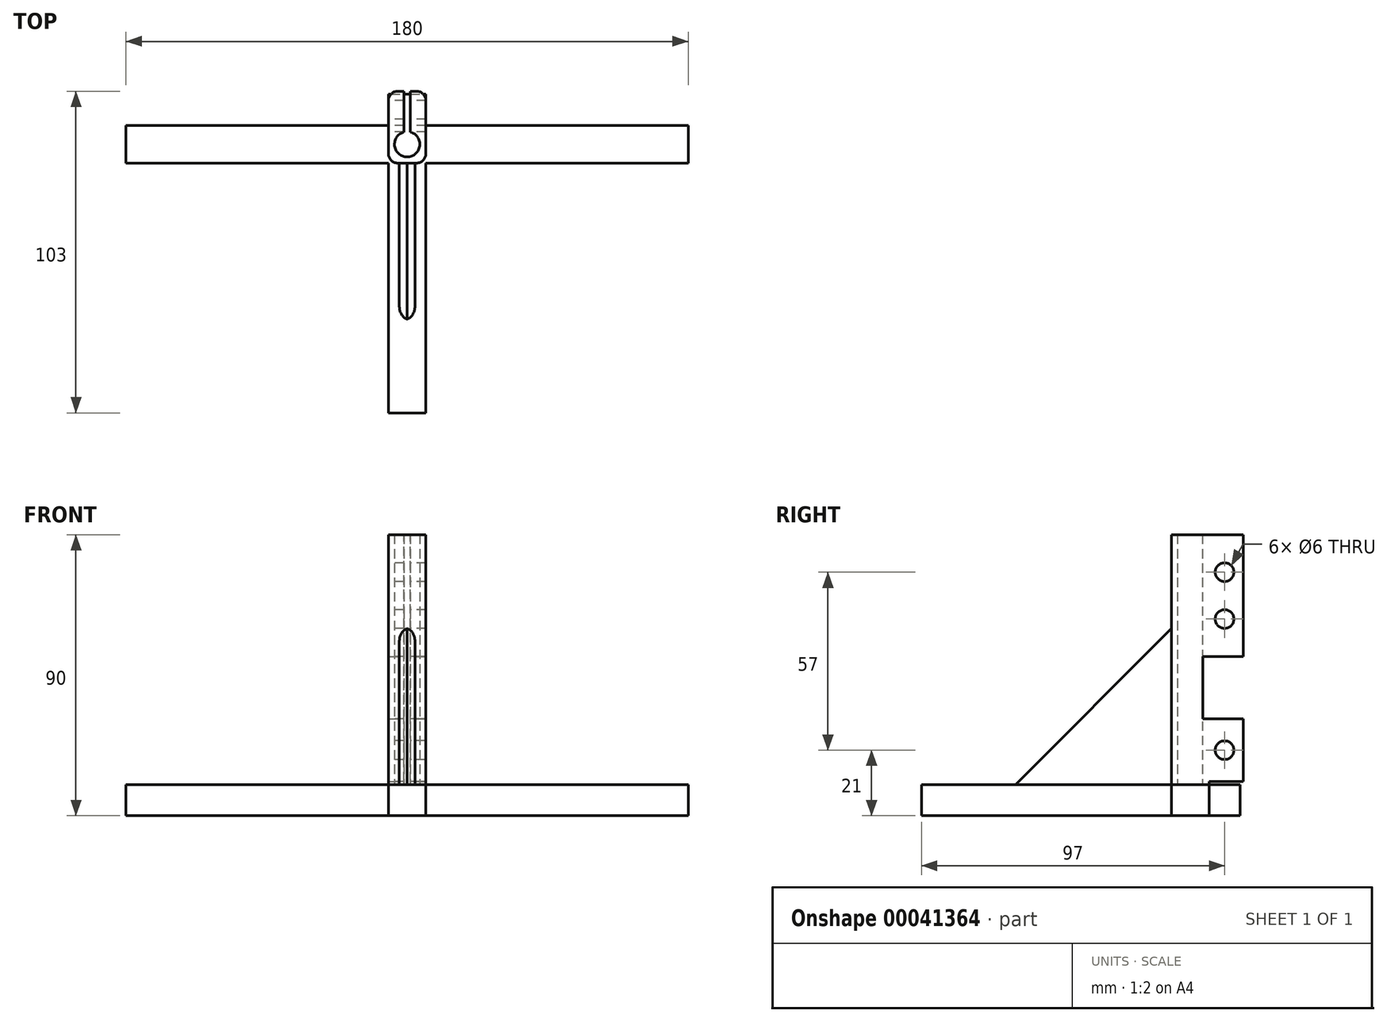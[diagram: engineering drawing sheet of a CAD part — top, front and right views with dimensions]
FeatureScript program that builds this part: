
annotation { "Feature Type Name" : "Feature", "Feature Type Description" : "" }
export const myFeature = defineFeature(function(context is Context, id is Id, definition is map)
    precondition{}
    {
        {
            var Q0;
            Q0=qCreatedBy(makeId("Top.planeOp"),FACE);
            var sketch = newSketch(context, id + "F0", { "sketchPlane" : qUnion([Q0])});
            skLineSegment(sketch, "E0", {"start": v(0, 22) * mm, "end": v(-6, 22) * mm});
            skLineSegment(sketch, "E1", {"start": v(-6, 22) * mm, "end": v(-6, 12) * mm});
            skLineSegment(sketch, "E2", {"start": v(-6, 12) * mm, "end": v(-90, 12) * mm});
            skLineSegment(sketch, "E3", {"start": v(-90, 12) * mm, "end": v(-90, 0) * mm});
            skLineSegment(sketch, "E4.MirrorCS", {"start": v(90, 12) * mm, "end": v(90, 0) * mm});
            skLineSegment(sketch, "E5.MirrorCS", {"start": v(6, 12) * mm, "end": v(90, 12) * mm});
            skLineSegment(sketch, "E6.MirrorCS", {"start": v(0, 22) * mm, "end": v(6, 22) * mm});
            skLineSegment(sketch, "E7.MirrorCS", {"start": v(6, 22) * mm, "end": v(6, 12) * mm});
            skLineSegment(sketch, "E8", {"start": v(-90, 0) * mm, "end": v(-6, 0) * mm});
            skLineSegment(sketch, "E9", {"start": v(-6, 0) * mm, "end": v(-6, -80) * mm});
            skLineSegment(sketch, "E10", {"start": v(-6, -80) * mm, "end": v(6, -80) * mm});
            skLineSegment(sketch, "E11", {"start": v(6, -80) * mm, "end": v(6, 0) * mm});
            skLineSegment(sketch, "E12", {"start": v(6, 0) * mm, "end": v(90, 0) * mm});
            skSolve(sketch);
        }
        {
            var Q0;
            Q0 = qSketchRegion(id + "F0", true);
            extrude(context, id + "F1", {"entities" : qUnion([Q0]), "depth" : 10 * mm});
        }
        {
            var Q0;
            Q0=makeQuery(id+"F1.opExtrude","CAP_FACE",FACE,{"disambiguationData":[OSD([sQuery(id+"F0.wireOp",EDGE,"E0"),sQuery(id+"F0.wireOp",EDGE,"E1"),sQuery(id+"F0.wireOp",EDGE,"E2"),sQuery(id+"F0.wireOp",EDGE,"E3"),sQuery(id+"F0.wireOp",EDGE,"198ae0ac-48d3-4eb9-aa4b-bc29fb24422c"),sQuery(id+"F0.wireOp",EDGE,"9f05f684-929d-4ba8-9fca-e720e47223410.MirrorCS"),sQuery(id+"F0.wireOp",EDGE,"E4.MirrorCS"),sQuery(id+"F0.wireOp",EDGE,"E5.MirrorCS"),sQuery(id+"F0.wireOp",EDGE,"E6.MirrorCS"),sQuery(id+"F0.wireOp",EDGE,"E7.MirrorCS")])],"isStart":false});
            var sketch = newSketch(context, id + "F2", { "sketchPlane" : qUnion([Q0])});
            skSolve(sketch);
        }
        {
            var Q0;
            Q0=makeQuery(id+"F2.imprint","IMPRINT",FACE,{"disambiguationData":[TD([[makeQuery(id+"F2.imprint","IMPRINT",EDGE,{"derivedFrom":makeQuery(id+"F1.opExtrude","CAP_EDGE",EDGE,{"disambiguationData":[OSD([sQuery(id+"F0.wireOp",EDGE,"E1")])],"isStart":false})}),1.0]])]});
            var sketch = newSketch(context, id + "F3", { "sketchPlane" : qUnion([Q0])});
            skLineSegment(sketch, "E13.rect.bottom", {"start": v(-6, 0) * mm, "end": v(6, 0) * mm});
            skLineSegment(sketch, "E13.rect.top", {"start": v(-6, 23) * mm, "end": v(6, 23) * mm});
            skLineSegment(sketch, "E13.rect.left", {"start": v(-6, 0) * mm, "end": v(-6, 23) * mm});
            skLineSegment(sketch, "E13.rect.right", {"start": v(6, 0) * mm, "end": v(6, 23) * mm});
            skPoint(sketch, "E13.rect.middle", {"position": v(0, 11.5) * mm});
            skCircle(sketch, "E14", {"center": v(0, 6) * mm, "radius": 4.05 * mm});
            skSolve(sketch);
        }
        {
            var Q0;
            Q0 = qSketchRegion(id + "F3", true);
            extrude(context, id + "F4", {"entities" : qUnion([Q0]), "operationType" : NewBodyOperationType.ADD, "depth" : 80 * mm});
        }
        {
            var Q0;
            Q0=makeQuery(id+"F2.imprint","IMPRINT",FACE,{"disambiguationData":[TD([[makeQuery(id+"F2.imprint","IMPRINT",EDGE,{"derivedFrom":makeQuery(id+"F1.opExtrude","CAP_EDGE",EDGE,{"disambiguationData":[OSD([sQuery(id+"F0.wireOp",EDGE,"E1")])],"isStart":false})}),1.0]])]});
            var sketch = newSketch(context, id + "F5", { "sketchPlane" : qUnion([Q0])});
            skLineSegment(sketch, "E15.rect.bottom", {"start": v(1, 6.26) * mm, "end": v(-1, 6.26) * mm});
            skLineSegment(sketch, "E15.rect.top", {"start": v(1, 45.32) * mm, "end": v(-1, 45.32) * mm});
            skLineSegment(sketch, "E15.rect.left", {"start": v(1, 6.26) * mm, "end": v(1, 45.32) * mm});
            skLineSegment(sketch, "E15.rect.right", {"start": v(-1, 6.26) * mm, "end": v(-1, 45.32) * mm});
            skPoint(sketch, "E15.rect.middle", {"position": v(0, 25.79) * mm});
            skPoint(sketch, "E15.rect.middle.positionSnap0", {"position": v(0, 23) * mm});
            skPoint(sketch, "E15.rect.centerSnap0", {"position": v(0, 23) * mm});
            skSolve(sketch);
        }
        {
            var Q0;
            Q0 = qSketchRegion(id + "F5", true);
            var Q1;
            Q1=makeQuery(id+"F4.opExtrude","CAP_FACE",FACE,{"disambiguationData":[OSD([sQuery(id+"F3.wireOp",EDGE,"E13.rect.bottom"),sQuery(id+"F3.wireOp",EDGE,"E13.rect.top"),sQuery(id+"F3.wireOp",EDGE,"E13.rect.left"),sQuery(id+"F3.wireOp",EDGE,"E13.rect.right"),sQuery(id+"F3.wireOp",EDGE,"E14")])],"isStart":false});
            extrude(context, id + "F6", {"entities" : qUnion([Q0]), "operationType" : NewBodyOperationType.REMOVE, "endBound" : BoundingType.UP_TO_SURFACE, "endBoundEntityFace" : qUnion([Q1]), "depth" : 25 * mm});
        }
        {
            var Q0;
            Q0=makeQuery(id+"F4.boolean.opBoolean","MERGE",FACE,{"derivedFrom":[makeQuery(id+"F1.opExtrude","SWEPT_FACE",FACE,{"disambiguationData":[OSD([sQuery(id+"F0.wireOp",EDGE,"E1")])]}),makeQuery(id+"F4.opExtrude","SWEPT_FACE",FACE,{"disambiguationData":[OSD([sQuery(id+"F3.wireOp",EDGE,"E13.rect.left")])]})]});
            var sketch = newSketch(context, id + "F7", { "sketchPlane" : qUnion([Q0])});
            skLineSegment(sketch, "E16.bottom", {"start": v(-23, 10) * mm, "end": v(-12, 10) * mm});
            skLineSegment(sketch, "E16.top", {"start": v(-23, 11) * mm, "end": v(-12, 11) * mm});
            skLineSegment(sketch, "E16.left", {"start": v(-23, 10) * mm, "end": v(-23, 11) * mm});
            skLineSegment(sketch, "E16.right", {"start": v(-12, 10) * mm, "end": v(-12, 11) * mm});
            skLineSegment(sketch, "E17.bottom", {"start": v(-23, 31) * mm, "end": v(-10, 31) * mm});
            skLineSegment(sketch, "E17.top", {"start": v(-23, 51) * mm, "end": v(-10, 51) * mm});
            skLineSegment(sketch, "E17.left", {"start": v(-23, 31) * mm, "end": v(-23, 51) * mm});
            skLineSegment(sketch, "E17.right", {"start": v(-10, 31) * mm, "end": v(-10, 51) * mm});
            skCircle(sketch, "E18", {"center": v(-17, 21) * mm, "radius": 3 * mm});
            skCircle(sketch, "E19", {"center": v(-17, 78) * mm, "radius": 3 * mm});
            skCircle(sketch, "E20", {"center": v(-17, 63) * mm, "radius": 3 * mm});
            skSolve(sketch);
        }
        {
            var Q0;
            Q0 = qSketchRegion(id + "F7", true);
            extrude(context, id + "F8", {"entities" : qUnion([Q0]), "operationType" : NewBodyOperationType.REMOVE, "oppositeDirection" : true, "depth" : 25 * mm});
        }
        {
            var Q0;
            Q0=qCreatedBy(makeId("Right.planeOp"),FACE);
            var sketch = newSketch(context, id + "F9", { "sketchPlane" : qUnion([Q0])});
            skLineSegment(sketch, "E21", {"start": v(0, 60) * mm, "end": v(-50, 10) * mm});
            skLineSegment(sketch, "E22", {"start": v(-50, 10) * mm, "end": v(0, 10) * mm});
            skLineSegment(sketch, "E23", {"start": v(0, 10) * mm, "end": v(0, 60) * mm});
            skSolve(sketch);
        }
        {
            var Q0;
            Q0 = qSketchRegion(id + "F9", true);
            extrude(context, id + "F10", {"entities" : qUnion([Q0]), "operationType" : NewBodyOperationType.ADD, "endBound" : BoundingType.SYMMETRIC, "depth" : 5 * mm});
        }
        {
            var Q0;
            Q0=makeQuery(id+"F4.opExtrude","SWEPT_EDGE",EDGE,{"disambiguationData":[OSD([sQuery(id+"F0.wireOp",EDGE,"198ae0ac-48d3-4eb9-aa4b-bc29fb24422c"),sQuery(id+"F0.wireOp",EDGE,"9f05f684-929d-4ba8-9fca-e720e47223410.MirrorCS"),sQuery(id+"F3.wireOp",EDGE,"E13.rect.bottom"),sQuery(id+"F3.wireOp",EDGE,"E13.rect.left")])]});
            var Q1;
            Q1=makeQuery(id+"F4.opExtrude","SWEPT_EDGE",EDGE,{"disambiguationData":[OSD([sQuery(id+"F0.wireOp",EDGE,"198ae0ac-48d3-4eb9-aa4b-bc29fb24422c"),sQuery(id+"F0.wireOp",EDGE,"9f05f684-929d-4ba8-9fca-e720e47223410.MirrorCS"),sQuery(id+"F3.wireOp",EDGE,"E13.rect.bottom"),sQuery(id+"F3.wireOp",EDGE,"E13.rect.right")])]});
            var Q2;
            {var subQ0=sQuery(id+"F0.wireOp",EDGE,"E1");var subQ1=sQuery(id+"F3.wireOp",EDGE,"E13.rect.top");var subQ2=sQuery(id+"F3.wireOp",EDGE,"E13.rect.left");Q2=makeQuery(id+"F8.boolean.opBoolean","SPLIT",EDGE,{"disambiguationData":[TD([makeQuery(id+"F8.opExtrude","SWEPT_FACE",FACE,{"disambiguationData":[OSD([sQuery(id+"F7.wireOp",EDGE,"E17.top")])]})])],"derivedFrom":makeQuery(id+"F4.opExtrude","SWEPT_EDGE",EDGE,{"disambiguationData":[OSD([subQ0,subQ1,subQ2])]})});}
            var Q3;
            {var subQ0=sQuery(id+"F0.wireOp",EDGE,"E7.MirrorCS");var subQ1=sQuery(id+"F3.wireOp",EDGE,"E13.rect.top");var subQ2=sQuery(id+"F3.wireOp",EDGE,"E13.rect.right");Q3=makeQuery(id+"F8.boolean.opBoolean","SPLIT",EDGE,{"disambiguationData":[TD([makeQuery(id+"F8.opExtrude","SWEPT_FACE",FACE,{"disambiguationData":[OSD([sQuery(id+"F7.wireOp",EDGE,"E17.top")])]})])],"derivedFrom":makeQuery(id+"F4.opExtrude","SWEPT_EDGE",EDGE,{"disambiguationData":[OSD([subQ0,subQ1,subQ2])]})});}
            var Q4;
            {var subQ0=sQuery(id+"F0.wireOp",EDGE,"E7.MirrorCS");var subQ1=sQuery(id+"F3.wireOp",EDGE,"E13.rect.top");var subQ2=sQuery(id+"F3.wireOp",EDGE,"E13.rect.right");Q4=makeQuery(id+"F8.boolean.opBoolean","SPLIT",EDGE,{"disambiguationData":[TD([makeQuery(id+"F8.opExtrude","SWEPT_FACE",FACE,{"disambiguationData":[OSD([sQuery(id+"F7.wireOp",EDGE,"E16.top")])]})])],"derivedFrom":makeQuery(id+"F4.opExtrude","SWEPT_EDGE",EDGE,{"disambiguationData":[OSD([subQ0,subQ1,subQ2])]})});}
            var Q5;
            {var subQ0=sQuery(id+"F0.wireOp",EDGE,"E1");var subQ1=sQuery(id+"F3.wireOp",EDGE,"E13.rect.top");var subQ2=sQuery(id+"F3.wireOp",EDGE,"E13.rect.left");Q5=makeQuery(id+"F8.boolean.opBoolean","SPLIT",EDGE,{"disambiguationData":[TD([makeQuery(id+"F8.opExtrude","SWEPT_FACE",FACE,{"disambiguationData":[OSD([sQuery(id+"F7.wireOp",EDGE,"E16.top")])]})])],"derivedFrom":makeQuery(id+"F4.opExtrude","SWEPT_EDGE",EDGE,{"disambiguationData":[OSD([subQ0,subQ1,subQ2])]})});}
            var Q6;
            Q6=makeQuery(id+"F10.opExtrude","CAP_EDGE",EDGE,{"disambiguationData":[OSD([sQuery(id+"F9.wireOp",EDGE,"E21")])],"isStart":true});
            var Q7;
            Q7=makeQuery(id+"F10.opExtrude","CAP_EDGE",EDGE,{"disambiguationData":[OSD([sQuery(id+"F9.wireOp",EDGE,"E21")])],"isStart":false});
            fillet(context, id + "F11", {"entities" : qUnion([Q0, Q1, Q2, Q3, Q4, Q5, Q6, Q7]), "radius" : 3 * mm, "tangentPropagation" : true, "allowEdgeOverflow" : false});
        }
    });
